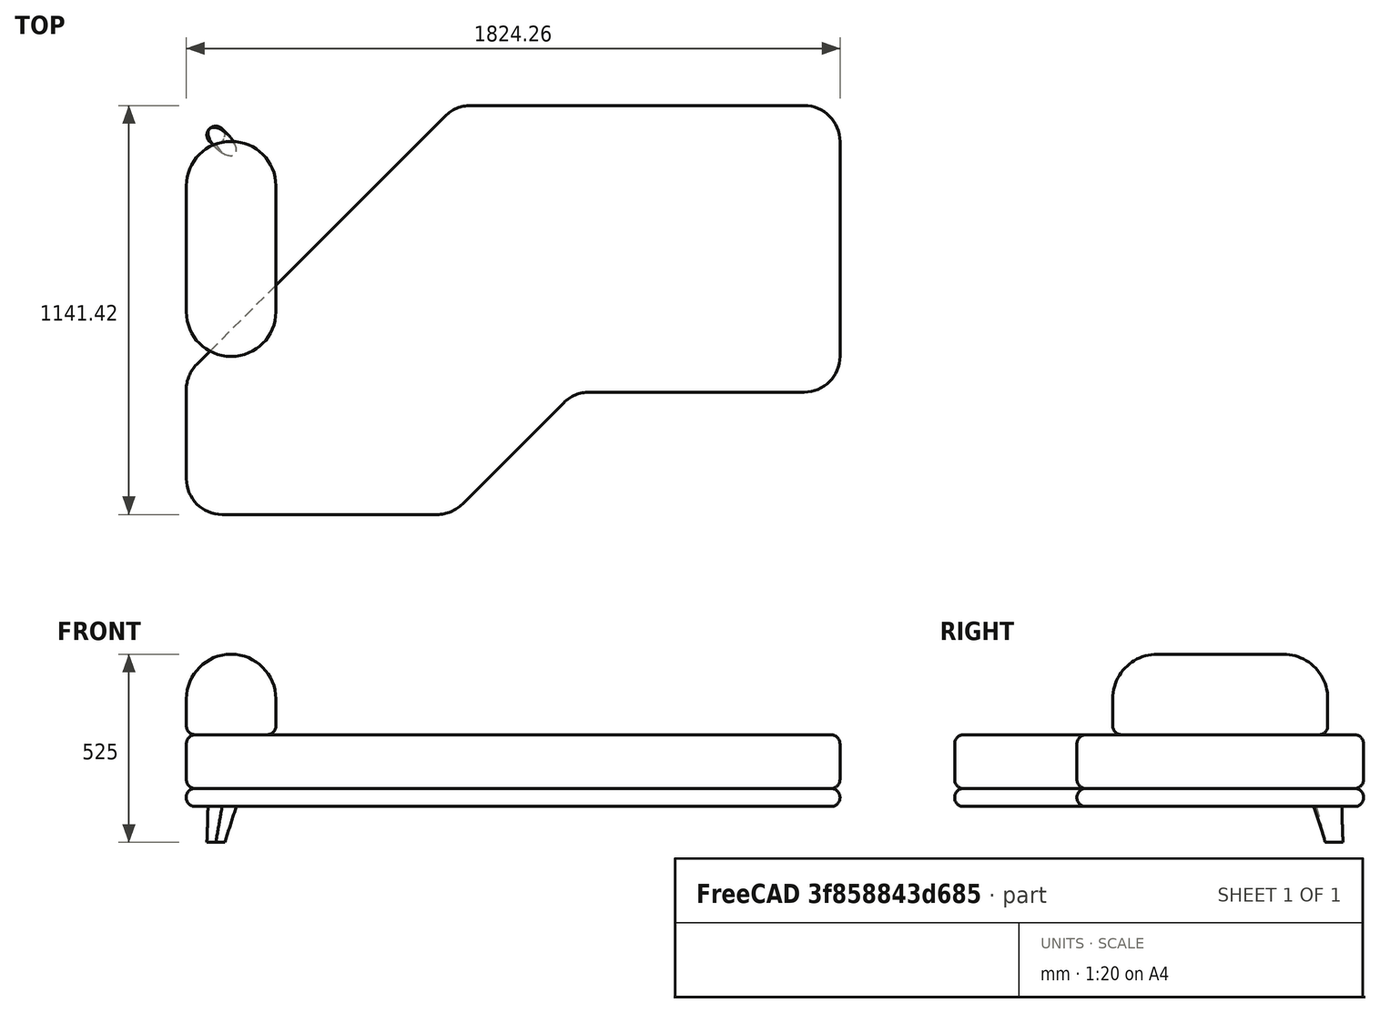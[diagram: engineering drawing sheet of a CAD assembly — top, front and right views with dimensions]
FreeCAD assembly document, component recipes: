
FREECAD ASSEMBLY — COMPONENT RECIPES ("Drawing room Sofa corner")

This assembly document has 10 components, labeled P0..P9 below (a component is one placed body or linked part). 10 of them carry a construction recipe — the FreeCAD feature program that regenerates the part from scratch, quoted from this document or its linked companion documents; the rest are supplied as boundary geometry only. No exploded tour is included for this assembly.
COMPONENT P0 — recipe-attached ("Backrest001", modeled in this document).
Construction recipe (the document's own serialized feature program — sketch geometry with constraints, then the solid features built on it; lengths are millimeters unless a unit is written):

FEATURE [Sketcher::SketchObject] Sketch002
  ArcFitTolerance = 1e-06
  AttachmentSupport = -> [XZ_Plane002]
  FullyConstrained = true
  MakeInternals = false
  MapMode = 5
  Placement = pos=(0,0,0) rot=(1,0,0;1.5708rad)
  sketch-geometry (5):
    g0: LineSegment StartX=0 StartY=0 StartZ=0 EndX=250 EndY=0 EndZ=0
    g1: LineSegment StartX=250 StartY=0 StartZ=0 EndX=250 EndY=100 EndZ=0
    g2: LineSegment [constr] StartX=250 StartY=100 StartZ=0 EndX=0 EndY=100 EndZ=0
    g3: LineSegment StartX=0 StartY=100 StartZ=0 EndX=0 EndY=0 EndZ=0
    g4: ArcOfCircle CenterX=125 CenterY=100 CenterZ=0 NormalX=0 NormalY=0 NormalZ=1 AngleXU=0 Radius=125 StartAngle=0 EndAngle=3.14159
  constraints (14):
    c: Coincident(g0,g1)
    c: Coincident(g1,g2)
    c: Coincident(g2,g3)
    c: Coincident(g3,g0)
    c: Horizontal(g0)
    c: Horizontal(g2)
    c: Vertical(g1)
    c: Vertical(g3)
    c: Distance(g1,g3) = 250
    c: Distance(g0,g2) = 100
    c: Coincident(g0,g-1)
    c: Coincident(g4,g2)
    c: Coincident(g4,g1)
    c: PointOnObject(g4,g2)
FEATURE [PartDesign::Pad] Pad002
  Direction = (0,-1,2e-16)
  Length = 600
  Length2 = 10
  Placement = pos=(0,0,0) rot=(1,0,0;1.5708rad)
  Profile = -> Sketch002
  ReferenceAxis = -> Sketch002 [N_Axis]
  Refine = true
  Suppressed = false
  Type = 0
FEATURE [PartDesign::Fillet] Fillet002
  Base = -> Pad002 [Edge9,Edge10]
  BaseFeature = -> Pad002
  Placement = pos=(0,0,0) rot=(1,0,0;1.5708rad)
  Radius = 124
  Refine = true
  SupportTransform = false
  Suppressed = false
  UseAllEdges = false
FEATURE [PartDesign::Fillet] Fillet003
  Base = -> Fillet002 [Face1]
  BaseFeature = -> Fillet002
  Placement = pos=(0,0,0) rot=(1,0,0;1.5708rad)
  Radius = 25
  Refine = true
  SupportTransform = false
  Suppressed = false
  UseAllEdges = true
FEATURE [PartDesign::Body] Body002  label="Backrest"
  AllowCompound = false
  Group = -> [Sketch002,Pad002,Fillet002,Fillet003]
  Origin = -> Origin002
  Placement = pos=(0,-100,200) rot=(0,0,1;0rad)
  Tip = -> Fillet003
COMPONENT P1 — same part as P0; its construction recipe is shown at P0.
COMPONENT P2 — recipe-attached ("Base001", modeled in this document).
Construction recipe (the document's own serialized feature program — sketch geometry with constraints, then the solid features built on it; lengths are millimeters unless a unit is written):

FEATURE [Sketcher::SketchObject] Sketch
  ArcFitTolerance = 1e-06
  AttachmentSupport = -> [XY_Plane]
  FullyConstrained = true
  MakeInternals = false
  MapMode = 5
  sketch-geometry (15):
    g0: ArcOfCircle CenterX=1724.26 CenterY=-100 CenterZ=0 NormalX=0 NormalY=0 NormalZ=1 AngleXU=0 Radius=100 StartAngle=1e-16 EndAngle=1.5708
    g1: LineSegment StartX=1824.26 StartY=-100 StartZ=0 EndX=1824.26 EndY=-700 EndZ=0
    g2: ArcOfCircle CenterX=1724.26 CenterY=-700 CenterZ=0 NormalX=0 NormalY=0 NormalZ=1 AngleXU=0 Radius=100 StartAngle=4.71239 EndAngle=6.28319
    g3: LineSegment StartX=1724.26 StartY=-800 StartZ=0 EndX=1124.26 EndY=-800 EndZ=0
    g4: ArcOfCircle CenterX=1124.26 CenterY=-900 CenterZ=0 NormalX=0 NormalY=0 NormalZ=1 AngleXU=0 Radius=100 StartAngle=1.5708 EndAngle=2.35619
    g5: LineSegment StartX=1053.55 StartY=-829.289 StartZ=0 EndX=770.711 EndY=-1112.13 EndZ=0
    g6: ArcOfCircle CenterX=700 CenterY=-1041.42 CenterZ=0 NormalX=0 NormalY=0 NormalZ=1 AngleXU=0 Radius=100 StartAngle=4.71239 EndAngle=5.49779
    g7: ArcOfCircle CenterX=100 CenterY=-792.893 CenterZ=0 NormalX=0 NormalY=0 NormalZ=1 AngleXU=0 Radius=100 StartAngle=2.35619 EndAngle=3.14159
    g8: LineSegment StartX=29.2893 StartY=-722.183 StartZ=0 EndX=722.183 EndY=-29.2893 EndZ=0
    g9: ArcOfCircle CenterX=792.893 CenterY=-100 CenterZ=0 NormalX=0 NormalY=0 NormalZ=1 AngleXU=0 Radius=100 StartAngle=1.5708 EndAngle=2.35619
    g10: LineSegment StartX=1724.26 StartY=0 StartZ=0 EndX=792.893 EndY=0 EndZ=0
    g11: LineSegment StartX=700 StartY=-1141.42 StartZ=0 EndX=100 EndY=-1141.42 EndZ=0
    g12: ArcOfCircle CenterX=100 CenterY=-1041.42 CenterZ=0 NormalX=0 NormalY=0 NormalZ=1 AngleXU=0 Radius=100 StartAngle=3.14159 EndAngle=4.71239
    g13: LineSegment StartX=0 StartY=-1041.42 StartZ=0 EndX=0 EndY=-792.893 EndZ=0
    g14: LineSegment [constr] StartX=0 StartY=-751.472 StartZ=0 EndX=751.472 EndY=-1.369e-13 EndZ=0
  constraints (42):
    c: Tangent(g0,g1) = 1.5708
    c: Tangent(g1,g2) = 1.5708
    c: Tangent(g2,g3) = 1.5708
    c: Tangent(g3,g4) = -1.5708
    c: Tangent(g4,g5) = -1.5708
    c: Tangent(g5,g6) = 1.5708
    c: Tangent(g7,g8) = 1.5708
    c: Tangent(g8,g9) = 1.5708
    c: Tangent(g10,g0) = -1.5708
    c: Tangent(g9,g10) = -1.5708
    c: Horizontal(g10)
    c: Vertical(g1)
    c: Horizontal(g3)
    c: Angle(g4) = 0.785398
    c: Radius(g2) = 100
    c: Radius(g0) = 100
    c: Radius(g9) = 100
    c: Parallel(g8,g5)
    c: Radius(g6) = 100
    c: Radius(g7) = 100
    c: Radius(g4) = 100
    c: Tangent(g6,g11) = 1.5708
    c: Tangent(g11,g12) = 1.5708
    c: Tangent(g12,g13) = 1.5708
    c: Vertical(g13)
    c: Horizontal(g11)
    c: Tangent(g7,g13) = 1.5708
    c: Radius(g12) = 100
    c: Distance(g1) = 600
    c: Distance(g11) = 600
    c: Distance(g3) = 600
    c: Distance(g5) = 400
    c: PointOnObject(g9,g-1)
    c: PointOnObject(g7,g-2)
    c: Distance(g4,g8) = 800
    c: PointOnObject(g14,g-2)
    c: PointOnObject(g14,g-1)
    c: PointOnObject(g14,g8)
    c: PointOnObject(g14,g8)
    c: Distance(g14,g-1) = 751.472
    c: Distance(g0,g-2) = 1824.26
    c: Distance(g11,g-1) = 1141.42
FEATURE [PartDesign::Pad] Pad
  Direction = (0,0,1)
  Length = 50
  Length2 = 10
  Profile = -> Sketch
  ReferenceAxis = -> Sketch [N_Axis]
  Refine = true
  Suppressed = false
  Type = 0
FEATURE [PartDesign::Fillet] Fillet001
  Base = -> Pad [?Face10]
  BaseFeature = -> Pad
  Radius = 24
  Refine = true
  SupportTransform = false
  Suppressed = false
  UseAllEdges = true
FEATURE [PartDesign::Body] Body  label="Base"
  AllowCompound = false
  Group = -> [Sketch,Pad,Fillet001]
  Origin = -> Origin
  Tip = -> Fillet001
COMPONENT P3 — recipe-attached ("Cushion001", modeled in this document).
Construction recipe (the document's own serialized feature program — sketch geometry with constraints, then the solid features built on it; lengths are millimeters unless a unit is written):

FEATURE [Sketcher::SketchObject] Sketch001
  ArcFitTolerance = 1e-06
  AttachmentSupport = -> [XY_Plane001]
  FullyConstrained = true
  MakeInternals = false
  MapMode = 5
  sketch-geometry (14):
    g0: LineSegment StartX=792.893 StartY=0 StartZ=0 EndX=1724.26 EndY=0 EndZ=0
    g1: ArcOfCircle CenterX=1724.26 CenterY=-100 CenterZ=0 NormalX=0 NormalY=0 NormalZ=1 AngleXU=0 Radius=100 StartAngle=1e-16 EndAngle=1.5708
    g2: LineSegment StartX=1824.26 StartY=-100 StartZ=0 EndX=1824.26 EndY=-700 EndZ=0
    g3: ArcOfCircle CenterX=1724.26 CenterY=-700 CenterZ=0 NormalX=0 NormalY=0 NormalZ=1 AngleXU=0 Radius=100 StartAngle=4.71239 EndAngle=6.28319
    g4: LineSegment StartX=1724.26 StartY=-800 StartZ=0 EndX=1124.26 EndY=-800 EndZ=0
    g5: ArcOfCircle CenterX=1124.26 CenterY=-900 CenterZ=0 NormalX=0 NormalY=0 NormalZ=1 AngleXU=0 Radius=100 StartAngle=1.5708 EndAngle=2.35619
    g6: LineSegment StartX=1053.55 StartY=-829.289 StartZ=0 EndX=770.711 EndY=-1112.13 EndZ=0
    g7: ArcOfCircle CenterX=700 CenterY=-1041.42 CenterZ=0 NormalX=0 NormalY=0 NormalZ=1 AngleXU=0 Radius=100 StartAngle=4.71239 EndAngle=5.49779
    g8: LineSegment StartX=700 StartY=-1141.42 StartZ=0 EndX=100 EndY=-1141.42 EndZ=0
    g9: ArcOfCircle CenterX=100 CenterY=-1041.42 CenterZ=0 NormalX=0 NormalY=0 NormalZ=1 AngleXU=0 Radius=100 StartAngle=3.14159 EndAngle=4.71239
    g10: LineSegment StartX=0 StartY=-1041.42 StartZ=0 EndX=0 EndY=-792.893 EndZ=0
    g11: ArcOfCircle CenterX=100 CenterY=-792.893 CenterZ=0 NormalX=0 NormalY=0 NormalZ=1 AngleXU=0 Radius=100 StartAngle=2.35619 EndAngle=3.14159
    g12: LineSegment StartX=29.2893 StartY=-722.183 StartZ=0 EndX=722.183 EndY=-29.2893 EndZ=0
    g13: ArcOfCircle CenterX=792.893 CenterY=-100 CenterZ=0 NormalX=0 NormalY=0 NormalZ=1 AngleXU=0 Radius=100 StartAngle=1.5708 EndAngle=2.35619
  constraints (37):
    c: PointOnObject(g0,g-1)
    c: Horizontal(g0)
    c: Tangent(g0,g1) = 1.5708
    c: Tangent(g1,g2) = 1.5708
    c: Tangent(g2,g3) = 1.5708
    c: Tangent(g3,g4) = 1.5708
    c: Tangent(g4,g5) = -1.5708
    c: Tangent(g5,g6) = -1.5708
    c: Tangent(g6,g7) = 1.5708
    c: Tangent(g7,g8) = 1.5708
    c: Tangent(g8,g9) = 1.5708
    c: Tangent(g9,g10) = 1.5708
    c: Tangent(g10,g11) = 1.5708
    c: Tangent(g11,g12) = 1.5708
    c: Tangent(g12,g13) = 1.5708
    c: Tangent(g13,g0) = 1.5708
    c: Radius(g1) = 100
    c: Radius(g3) = 100
    c: Radius(g5) = 100
    c: Radius(g7) = 100
    c: Radius(g9) = 100
    c: Radius(g11) = 100
    c: Radius(g13) = 100
    c: Horizontal(g4)
    c: Vertical(g2)
    c: Vertical(g10)
    c: Horizontal(g8)
    c: Parallel(g12,g6)
    c: Angle(g5) = 0.785398
    c: Distance(g2) = 600
    c: Distance(g4) = 600
    c: Distance(g6) = 400
    c: Distance(g5,g12) = 800
    c: Distance(g8) = 600
    c: PointOnObject(g10,g-2)
    c: Distance(g12,g12) = 979.899
    c: DistanceX(g-1,g12) = 722.183
FEATURE [PartDesign::Pad] Pad001
  Direction = (0,0,1)
  Length = 150
  Length2 = 10
  Profile = -> Sketch001
  ReferenceAxis = -> Sketch001 [N_Axis]
  Refine = true
  Suppressed = false
  Type = 0
FEATURE [PartDesign::Fillet] Fillet
  Base = -> Pad001
  BaseFeature = -> Pad001
  Radius = 25
  Refine = true
  SupportTransform = false
  Suppressed = false
  UseAllEdges = true
FEATURE [PartDesign::Body] Body001  label="Cushion"
  AllowCompound = false
  Group = -> [Sketch001,Pad001,Fillet]
  Origin = -> Origin001
  Placement = pos=(0,0,50) rot=(0,0,1;0rad)
  Tip = -> Fillet
COMPONENT P4 — recipe-attached ("Legs001", modeled in this document).
Construction recipe (the document's own serialized feature program — sketch geometry with constraints, then the solid features built on it; lengths are millimeters unless a unit is written):

FEATURE [Sketcher::SketchObject] Sketch003
  ArcFitTolerance = 1e-06
  AttachmentSupport = -> [XY_Plane003]
  FullyConstrained = true
  MakeInternals = false
  MapMode = 5
  sketch-geometry (5):
    g0: Ellipse CenterX=0 CenterY=0 CenterZ=0 NormalX=0 NormalY=0 NormalZ=1 MajorRadius=50 MinorRadius=25 AngleXU=-2.35619
    g1: LineSegment [constr] StartX=-35.3553 StartY=-35.3553 StartZ=0 EndX=35.3553 EndY=35.3553 EndZ=0
    g2: LineSegment [constr] StartX=17.6777 StartY=-17.6777 StartZ=0 EndX=-17.6777 EndY=17.6777 EndZ=0
    g3: GeomPoint [constr] X=-30.6186 Y=-30.6186 Z=0
    g4: GeomPoint [constr] X=30.6186 Y=30.6186 Z=0
  constraints (5):
    c: InternalAlignment(g1-g4 -> g0) x4
    c: Distance(g0,g1) = 50
    c: Angle(g1) = 0.785398
    c: Distance(g0,g2) = 25
    c: Coincident(g0,g-1)
FEATURE [PartDesign::Plane] DatumPlane
  AttachmentOffset = pos=(0,0,-100) rot=(0,0,1;0rad)
  AttachmentSupport = -> [Sketch003]
  Length = 60
  MapMode = 2
  Placement = pos=(0,0,-100) rot=(0,0,1;0rad)
  ResizeMode = 0
  Width = 60
FEATURE [Sketcher::SketchObject] Sketch004
  ArcFitTolerance = 1e-06
  AttachmentSupport = -> [DatumPlane]
  FullyConstrained = true
  MakeInternals = false
  MapMode = 5
  Placement = pos=(0,0,-100) rot=(0,0,1;0rad)
  sketch-geometry (2):
    g0: Circle CenterX=-17.6777 CenterY=-17.6777 CenterZ=0 NormalX=0 NormalY=0 NormalZ=1 AngleXU=0 Radius=25
    g1: LineSegment [constr] StartX=-17.6777 StartY=-17.6777 StartZ=0 EndX=2.4e-15 EndY=4.5e-15 EndZ=0
  constraints (5):
    c: Diameter(g0) = 50
    c: Coincident(g1,g0)
    c: Coincident(g1,g-1)
    c: Angle(g1,g-1) = 2.35619
    c: PointOnObject(g1,g0)
FEATURE [PartDesign::AdditiveLoft] AdditiveLoft
  Closed = false
  Profile = -> Sketch003
  Refine = true
  Ruled = false
  Sections = -> [Sketch004]
  Suppressed = false
FEATURE [PartDesign::Body] Body003  label="Legs"
  AllowCompound = false
  Group = -> [Sketch003,DatumPlane,Sketch004,AdditiveLoft]
  Origin = -> Origin003
  Placement = pos=(100,-100,0) rot=(0,0,1;-1.5708rad)
  Tip = -> AdditiveLoft
COMPONENT P5 — same part as P4; its construction recipe is shown at P4.
COMPONENT P6 — same part as P4; its construction recipe is shown at P4.
COMPONENT P7 — same part as P4; its construction recipe is shown at P4.
COMPONENT P8 — same part as P4; its construction recipe is shown at P4.
COMPONENT P9 — same part as P4; its construction recipe is shown at P4.
PROVENANCE & LICENSES
A FreeCAD (.FCStd) document from a public repository crawl; recipes are the document's own serialized feature recipes (and, for linked parts, companion documents' recipes).
License: as declared in the source repository (recorded in the dataset sidecar).
